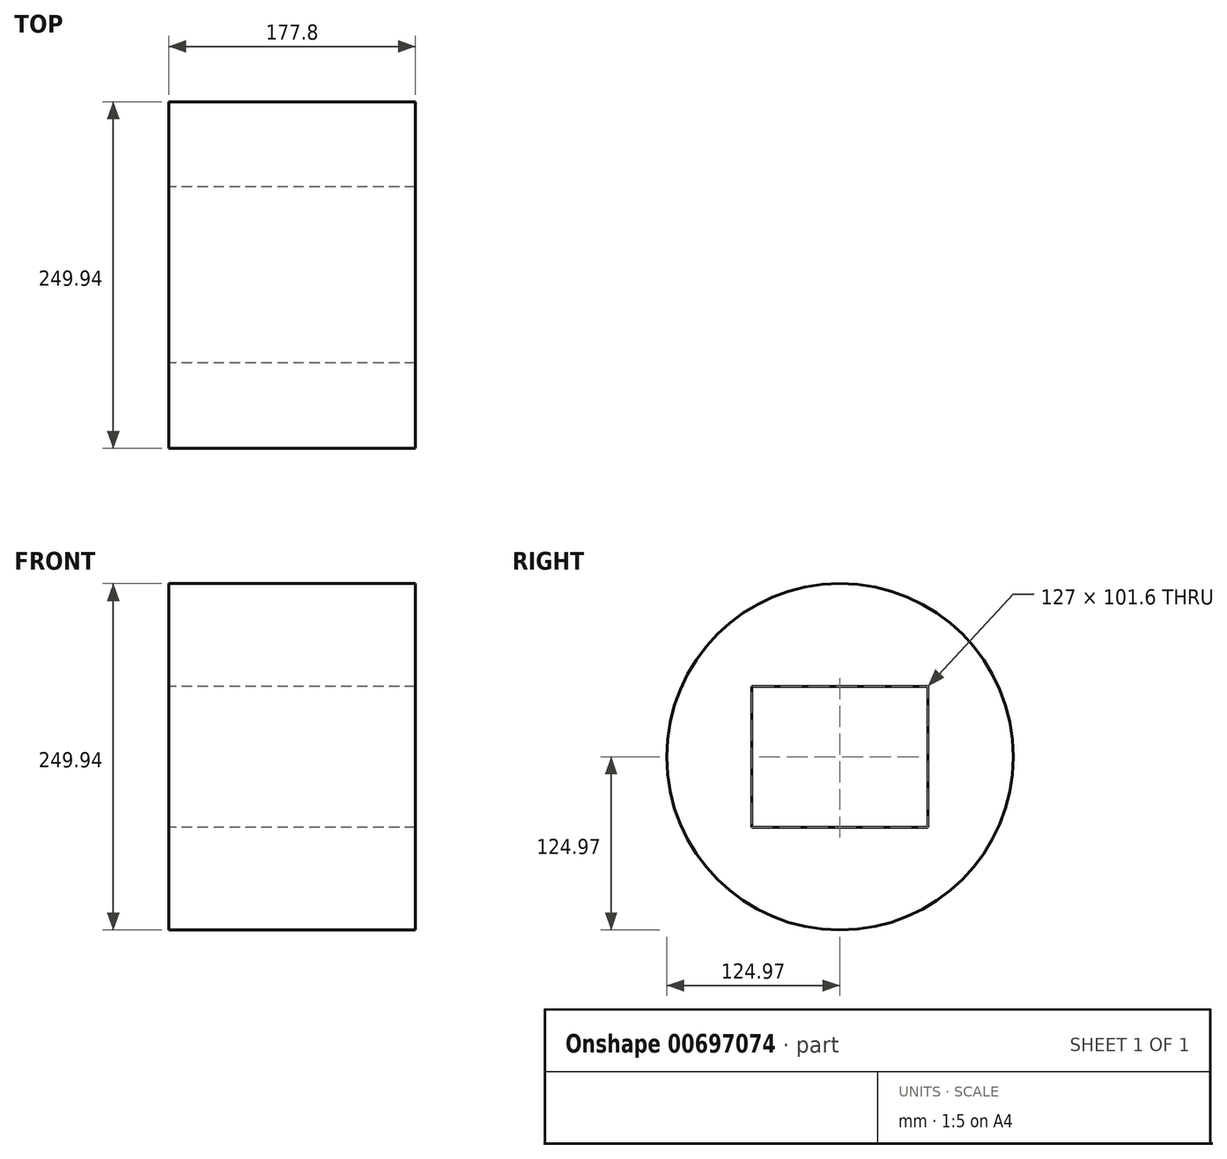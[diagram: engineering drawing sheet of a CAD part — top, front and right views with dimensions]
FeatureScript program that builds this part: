
annotation { "Feature Type Name" : "Feature", "Feature Type Description" : "" }
export const myFeature = defineFeature(function(context is Context, id is Id, definition is map)
    precondition{}
    {
        {
            var Q0;
            Q0=qCreatedBy(makeId("Right.planeOp"),FACE);
            var sketch = newSketch(context, id + "F0", { "sketchPlane" : qUnion([Q0])});
            skCircle(sketch, "E0", {"center": v(0, 0) * mm, "radius": 124.97 * mm});
            skLineSegment(sketch, "E1.bottom", {"start": v(63.5, -50.8) * mm, "end": v(-63.5, -50.8) * mm});
            skLineSegment(sketch, "E1.top", {"start": v(63.5, 50.8) * mm, "end": v(-63.5, 50.8) * mm});
            skLineSegment(sketch, "E1.left", {"start": v(63.5, -50.8) * mm, "end": v(63.5, 50.8) * mm});
            skLineSegment(sketch, "E1.right", {"start": v(-63.5, -50.8) * mm, "end": v(-63.5, 50.8) * mm});
            skSolve(sketch);
        }
        {
            var Q0;
            Q0 = qSketchRegion(id + "F0", true);
            extrude(context, id + "F1", {"entities" : qUnion([Q0]), "depth" : 177.8 * mm, "offsetDistance" : 25.4 * mm});
        }
    });
